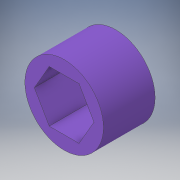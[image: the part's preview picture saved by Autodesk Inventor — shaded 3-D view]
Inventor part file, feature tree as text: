
AUTODESK INVENTOR PART (.ipt)
format: ipt  version: 2018 (Build 220112000, 112)  size: 107,008 bytes
history: native  units: in
note: dims shown in document units (in); Inventor stores cm internally (conversion verified against a paired STEP export)
features: extrude x1, sketch x1
ambient origin geometry x8: Origin, YZ Plane, XZ Plane, XY Plane, X Axis, Y Axis, Z Axis, Center Point
bodies: Solid1 (feature_tree)
feature tree (2):
  extrude  "Extrusion1"  Depth=0.5in
  sketch  "Sketch1"  dims[d0=0.5in d1=0.76in d2=0.5in d3=0.0in]
